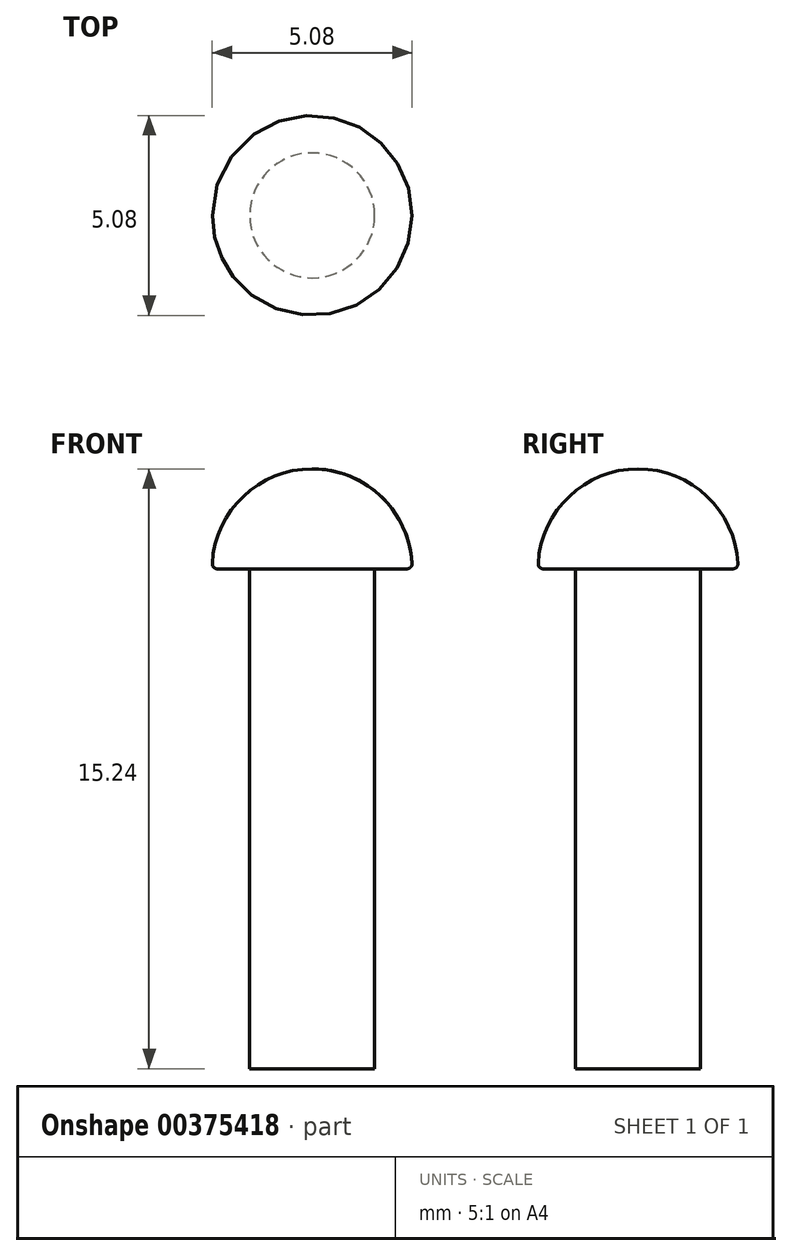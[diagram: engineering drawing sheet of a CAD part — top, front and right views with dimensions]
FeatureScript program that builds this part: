
annotation { "Feature Type Name" : "Feature", "Feature Type Description" : "" }
export const myFeature = defineFeature(function(context is Context, id is Id, definition is map)
    precondition{}
    {
        {
            var Q0;
            Q0=qCreatedBy(makeId("Front.planeOp"),FACE);
            var sketch = newSketch(context, id + "F0", { "sketchPlane" : qUnion([Q0])});
            skArc(sketch, "E0", {"start": v(2.54, 0) * mm, "mid": v(1.8, 1.8) * mm, "end": v(0, 2.54) * mm});
            skLineSegment(sketch, "E1", {"start": v(0, 0) * mm, "end": v(2.54, 0) * mm});
            skLineSegment(sketch, "E2", {"start": v(0, 0) * mm, "end": v(0, 2.54) * mm});
            skPoint(sketch, "E3.orphan", {"position": v(-2.54, 0) * mm});
            skSolve(sketch);
        }
        {
            var Q0;
            Q0=qSketchRegion(id+"F0",true);
            var Q1;
            Q1=sQuery(id+"F0.wireOp",EDGE,"E2");
            revolve(context, id + "F1", {"entities" : qUnion([Q0]), "axis" : qUnion([Q1]), "revolveType" : RevolveType.FULL});
        }
        {
            var Q0;
            Q0=makeQuery(id+"F1.opRevolve","SWEPT_FACE",FACE,{"disambiguationData":[OSD([sQuery(id+"F0.wireOp",EDGE,"E1")])]});
            var sketch = newSketch(context, id + "F2", { "sketchPlane" : qUnion([Q0])});
            skCircle(sketch, "E4", {"center": v(0, 0) * mm, "radius": 1.59 * mm});
            skSolve(sketch);
        }
        {
            var Q0;
            Q0=qSketchRegion(id+"F2",true);
            extrude(context, id + "F3", {"entities" : qUnion([Q0]), "operationType" : NewBodyOperationType.ADD, "depth" : 12.7 * mm});
        }
        {
            var Q0;
            Q0=makeQuery(id+"F1.opRevolve","SWEPT_EDGE",EDGE,{"disambiguationData":[OSD([sQuery(id+"F0.wireOp",EDGE,"E0"),sQuery(id+"F0.wireOp",EDGE,"E1")])]});
            fillet(context, id + "F4", {"entities" : qUnion([Q0]), "radius" : 0.13 * mm, "tangentPropagation" : true, "allowEdgeOverflow" : false});
        }
    });
